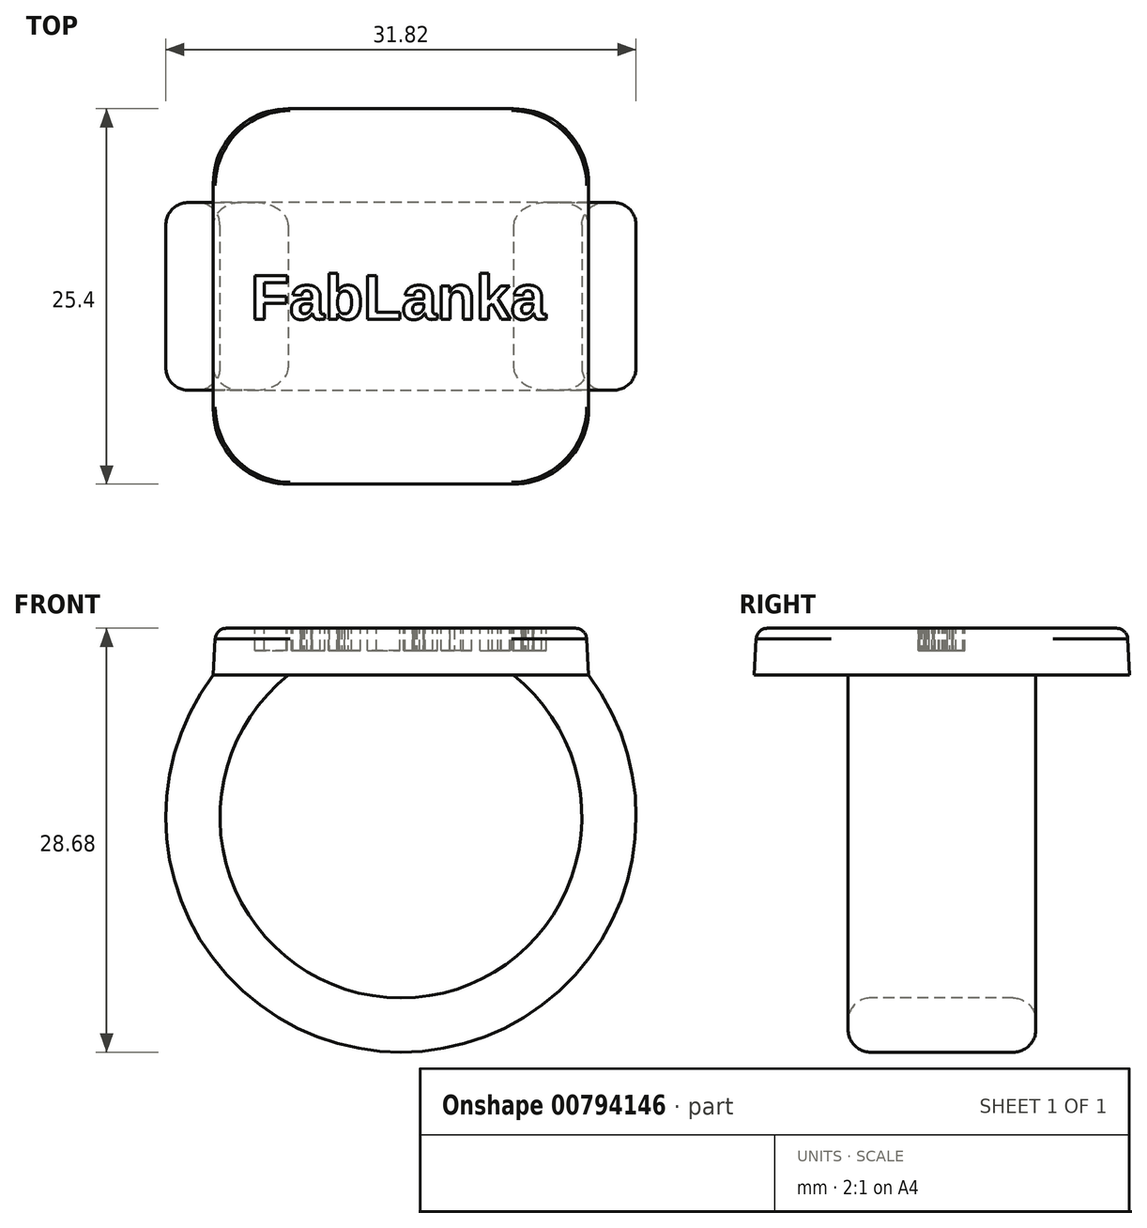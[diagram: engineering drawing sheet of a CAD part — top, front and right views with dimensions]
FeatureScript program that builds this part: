
annotation { "Feature Type Name" : "Feature", "Feature Type Description" : "" }
export const myFeature = defineFeature(function(context is Context, id is Id, definition is map)
    precondition{}
    {
        {
            var Q0;
            Q0=qCreatedBy(makeId("Top.planeOp"),FACE);
            var sketch = newSketch(context, id + "F0", { "sketchPlane" : qUnion([Q0])});
            skLineSegment(sketch, "E0.bottom", {"start": v(-12.7, 12.7) * mm, "end": v(12.7, 12.7) * mm});
            skLineSegment(sketch, "E0.top", {"start": v(-12.7, -12.7) * mm, "end": v(12.7, -12.7) * mm});
            skLineSegment(sketch, "E0.left", {"start": v(-12.7, 12.7) * mm, "end": v(-12.7, -12.7) * mm});
            skLineSegment(sketch, "E0.right", {"start": v(12.7, 12.7) * mm, "end": v(12.7, -12.7) * mm});
            skPoint(sketch, "E0.middle", {"position": v(0, 0) * mm});
            skSolve(sketch);
        }
        {
            var Q0;
            Q0 = qSketchRegion(id + "F0", true);
            extrude(context, id + "F1", {"entities" : qUnion([Q0]), "depth" : 3.17 * mm, "offsetDistance" : 25.4 * mm, "hasDraft" : true, "draftAngle" : 3 * degree, "draftPullDirection" : true});
        }
        {
            var Q0;
            Q0=qCreatedBy(makeId("Front.planeOp"),FACE);
            var sketch = newSketch(context, id + "F2", { "sketchPlane" : qUnion([Q0])});
            skArc(sketch, "E1", {"start": v(-10.16, 0) * mm, "mid": v(0, -23.56) * mm, "end": v(10.16, 0) * mm});
            skSolve(sketch);
        }
        {
            var Q0;
            Q0=makeQuery(id+"F1.opExtrude","CAP_FACE",FACE,{"disambiguationData":[OSD([sQuery(id+"F0.wireOp",EDGE,"E0.bottom"),sQuery(id+"F0.wireOp",EDGE,"E0.top"),sQuery(id+"F0.wireOp",EDGE,"E0.left"),sQuery(id+"F0.wireOp",EDGE,"E0.right")])],"isStart":true});
            var sketch = newSketch(context, id + "F3", { "sketchPlane" : qUnion([Q0])});
            skPoint(sketch, "E2.middle", {"position": v(-10.16, 0) * mm});
            skLineSegment(sketch, "E3.bottom", {"start": v(-7.62, -6.35) * mm, "end": v(-12.7, -6.35) * mm});
            skLineSegment(sketch, "E3.top", {"start": v(-7.62, 6.35) * mm, "end": v(-12.7, 6.35) * mm});
            skLineSegment(sketch, "E3.left", {"start": v(-7.62, -6.35) * mm, "end": v(-7.62, 6.35) * mm});
            skLineSegment(sketch, "E3.right", {"start": v(-12.7, -6.35) * mm, "end": v(-12.7, 6.35) * mm});
            skSolve(sketch);
        }
        {
            var Q0;
            Q0=makeQuery(id+"F3.imprint","IMPRINT",FACE,{"disambiguationData":[TD([[makeQuery(id+"F3.imprint","IMPRINT",EDGE,{"derivedFrom":sQuery(id+"F3.wireOp",EDGE,"E3.bottom")}),-1.0]])]});
            var Q1;
            Q1=sQuery(id+"F2.wireOp",EDGE,"E1");
            sweep(context, id + "F4", {"operationType" : NewBodyOperationType.ADD, "profiles" : qUnion([Q0]), "path" : qUnion([Q1])});
        }
        {
            var Q0;
            Q0=qCreatedBy(makeId("Front.planeOp"),FACE);
            var sketch = newSketch(context, id + "F5", { "sketchPlane" : qUnion([Q0])});
            skLineSegment(sketch, "E4.1", {"start": v(10.01, -2.54) * mm, "end": v(10.16, 0) * mm});
            skArc(sketch, "E4.2", {"start": v(10.01, -2.54) * mm, "mid": v(8.9, -1.18) * mm, "end": v(7.62, 0) * mm});
            skLineSegment(sketch, "E5.trimOffspring", {"start": v(7.62, 0) * mm, "end": v(10.16, 0) * mm});
            skPoint(sketch, "E6.orphan", {"position": v(12.7, 0) * mm});
            skSolve(sketch);
        }
        {
            var Q0;
            Q0=makeQuery(id+"F5.imprint","IMPRINT",FACE,{"disambiguationData":[TD([[makeQuery(id+"F5.imprint","IMPRINT",EDGE,{"derivedFrom":sQuery(id+"F5.wireOp",EDGE,"E4.1")}),1.0]])]});
            var Q1;
            Q1=makeQuery(id+"F4.opSweep","SWEPT_FACE",FACE,{"disambiguationData":[OSD([sQuery(id+"F2.wireOp",EDGE,"E1"),sQuery(id+"F3.wireOp",EDGE,"E3.bottom")])]});
            var Q2;
            Q2=makeQuery(id+"F4.opSweep","SWEPT_FACE",FACE,{"disambiguationData":[OSD([sQuery(id+"F2.wireOp",EDGE,"E1"),sQuery(id+"F3.wireOp",EDGE,"E3.top")])]});
            extrude(context, id + "F6", {"entities" : qUnion([Q0]), "operationType" : NewBodyOperationType.ADD, "endBound" : BoundingType.UP_TO_SURFACE, "oppositeDirection" : true, "depth" : 25.4 * mm, "endBoundEntityFace" : qUnion([Q1]), "offsetDistance" : 25.4 * mm, "hasSecondDirection" : true, "secondDirectionBound" : SecondDirectionBoundingType.UP_TO_SURFACE, "secondDirectionOppositeDirection" : false, "secondDirectionDepth" : 25.4 * mm, "secondDirectionBoundEntityFace" : qUnion([Q2])});
        }
        {
            var Q0;
            Q0=makeQuery(id+"F1.opExtrude","SWEPT_EDGE",EDGE,{"disambiguationData":[OSD([sQuery(id+"F0.wireOp",EDGE,"E0.top"),sQuery(id+"F0.wireOp",EDGE,"E0.left")])]});
            var Q1;
            Q1=makeQuery(id+"F1.opExtrude","SWEPT_EDGE",EDGE,{"disambiguationData":[OSD([sQuery(id+"F0.wireOp",EDGE,"E0.top"),sQuery(id+"F0.wireOp",EDGE,"E0.right")])]});
            var Q2;
            Q2=makeQuery(id+"F1.opExtrude","SWEPT_EDGE",EDGE,{"disambiguationData":[OSD([sQuery(id+"F0.wireOp",EDGE,"E0.bottom"),sQuery(id+"F0.wireOp",EDGE,"E0.right")])]});
            var Q3;
            Q3=makeQuery(id+"F1.opExtrude","SWEPT_EDGE",EDGE,{"disambiguationData":[OSD([sQuery(id+"F0.wireOp",EDGE,"E0.bottom"),sQuery(id+"F0.wireOp",EDGE,"E0.left")])]});
            fillet(context, id + "F7", {"entities" : qUnion([Q0, Q1, Q2, Q3]), "radius" : 5.08 * mm, "tangentPropagation" : true, "allowEdgeOverflow" : false});
        }
        {
            var Q0;
            Q0=makeQuery(id+"F6.boolean.opBoolean","MERGE",EDGE,{"derivedFrom":[makeQuery(id+"F4.opSweep","SWEPT_EDGE",EDGE,{"disambiguationData":[OSD([sQuery(id+"F2.wireOp",EDGE,"E1"),sQuery(id+"F3.wireOp",EDGE,"E3.top"),sQuery(id+"F3.wireOp",EDGE,"E3.left")])]}),makeQuery(id+"F6.opExtrude","CAP_EDGE",EDGE,{"disambiguationData":[OSD([sQuery(id+"F5.wireOp",EDGE,"E4.2")])],"isStart":true})]});
            var Q1;
            Q1=makeQuery(id+"F4.opSweep","SWEPT_EDGE",EDGE,{"disambiguationData":[OSD([sQuery(id+"F0.wireOp",EDGE,"E0.left"),sQuery(id+"F2.wireOp",EDGE,"E1"),sQuery(id+"F3.wireOp",EDGE,"E3.top"),sQuery(id+"F3.wireOp",EDGE,"E3.right")])]});
            var Q2;
            Q2=makeQuery(id+"F6.boolean.opBoolean","MERGE",EDGE,{"derivedFrom":[makeQuery(id+"F4.opSweep","SWEPT_EDGE",EDGE,{"disambiguationData":[OSD([sQuery(id+"F2.wireOp",EDGE,"E1"),sQuery(id+"F3.wireOp",EDGE,"E3.bottom"),sQuery(id+"F3.wireOp",EDGE,"E3.left")])]}),makeQuery(id+"F6.opExtrude","CAP_EDGE",EDGE,{"disambiguationData":[OSD([sQuery(id+"F5.wireOp",EDGE,"E4.2")])],"isStart":false})]});
            var Q3;
            Q3=makeQuery(id+"F4.opSweep","SWEPT_EDGE",EDGE,{"disambiguationData":[OSD([sQuery(id+"F0.wireOp",EDGE,"E0.left"),sQuery(id+"F2.wireOp",EDGE,"E1"),sQuery(id+"F3.wireOp",EDGE,"E3.bottom"),sQuery(id+"F3.wireOp",EDGE,"E3.right")])]});
            fillet(context, id + "F8", {"entities" : qUnion([Q0, Q1, Q2, Q3]), "radius" : 1.52 * mm, "tangentPropagation" : true, "allowEdgeOverflow" : false});
        }
        {
            var Q0;
            Q0=makeQuery(id+"F1.opExtrude","CAP_FACE",FACE,{"disambiguationData":[OSD([sQuery(id+"F0.wireOp",EDGE,"E0.bottom"),sQuery(id+"F0.wireOp",EDGE,"E0.top"),sQuery(id+"F0.wireOp",EDGE,"E0.left"),sQuery(id+"F0.wireOp",EDGE,"E0.right")])],"isStart":false});
            fillet(context, id + "F9", {"entities" : qUnion([Q0]), "radius" : 0.76 * mm, "tangentPropagation" : true, "allowEdgeOverflow" : false});
        }
        {
            var Q0;
            Q0=makeQuery(id+"F1.opExtrude","CAP_FACE",FACE,{"disambiguationData":[OSD([sQuery(id+"F0.wireOp",EDGE,"E0.bottom"),sQuery(id+"F0.wireOp",EDGE,"E0.top"),sQuery(id+"F0.wireOp",EDGE,"E0.left"),sQuery(id+"F0.wireOp",EDGE,"E0.right")])],"isStart":false});
            var sketch = newSketch(context, id + "F10", { "sketchPlane" : qUnion([Q0])});
            skText(sketch, "E7", { "text": "FabLanka", "fontName": "Arimo-Bold.ttf"});
            const initialGuessF10  = {"E7": [-0.01016, -0.00154, 1, 0, 0.00308]};
            skSetInitialGuess(sketch, initialGuessF10);
            skSolve(sketch);
        }
        {
            var Q0;
            Q0 = qSketchRegion(id + "F10", true);
            extrude(context, id + "F11", {"entities" : qUnion([Q0]), "operationType" : NewBodyOperationType.REMOVE, "oppositeDirection" : true, "depth" : 1.52 * mm, "offsetDistance" : 25.4 * mm});
        }
    });
